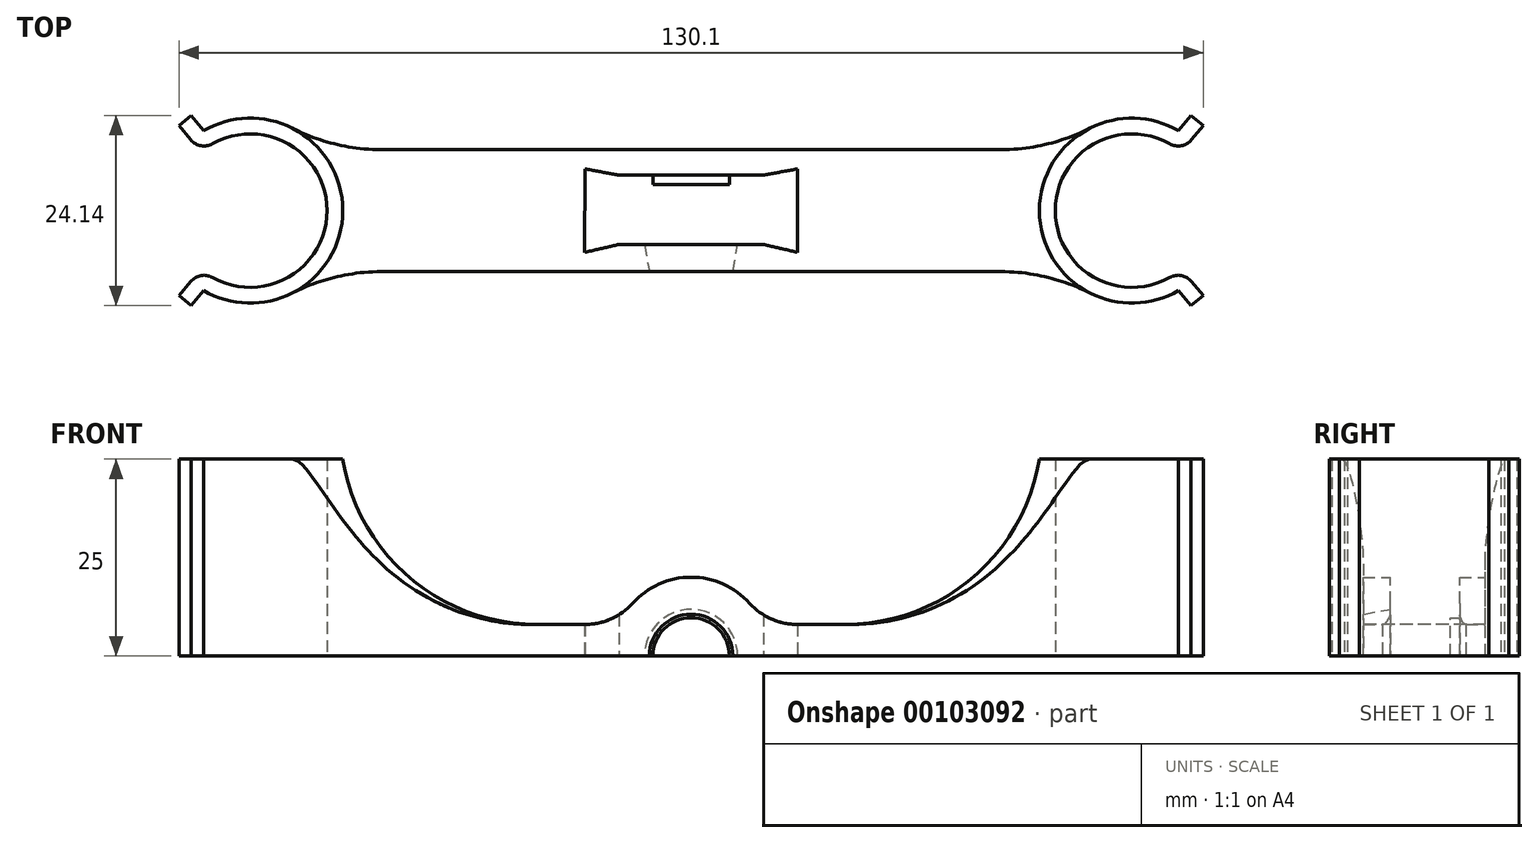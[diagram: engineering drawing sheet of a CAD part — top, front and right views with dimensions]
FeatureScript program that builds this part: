
annotation { "Feature Type Name" : "Feature", "Feature Type Description" : "" }
export const myFeature = defineFeature(function(context is Context, id is Id, definition is map)
    precondition{}
    {
        {
            var Q0;
            Q0=qCreatedBy(makeId("Top.planeOp"),FACE);
            var sketch = newSketch(context, id + "F0", { "sketchPlane" : qUnion([Q0])});
            skArc(sketch, "E0", {"start": v(-62.27, -7.47) * mm, "mid": v(-46.25, 0) * mm, "end": v(-62.27, 7.47) * mm});
            skLineSegment(sketch, "E1", {"start": v(-56, 0) * mm, "end": v(-68.54, -14.94) * mm, "construction": true});
            skLineSegment(sketch, "E2", {"start": v(-56, 0) * mm, "end": v(-67.56, 13.78) * mm, "construction": true});
            skArc(sketch, "E3", {"start": v(-63.55, -9) * mm, "mid": v(-44.25, 0) * mm, "end": v(-63.55, 9) * mm});
            skLineSegment(sketch, "E4", {"start": v(-63.55, 9) * mm, "end": v(-65.05, 10.78) * mm});
            skLineSegment(sketch, "E5", {"start": v(-65.05, 10.78) * mm, "end": v(-63.52, 12.07) * mm});
            skLineSegment(sketch, "E6", {"start": v(-63.52, 12.07) * mm, "end": v(-61.91, 10.16) * mm});
            skLineSegment(sketch, "E7", {"start": v(-54.18, 11.6) * mm, "end": v(-54.49, 9.63) * mm, "construction": true});
            skArc(sketch, "E8", {"start": v(-63.55, 9) * mm, "mid": v(-62.26, 8.25) * mm, "end": v(-60.78, 8.5) * mm});
            skLineSegment(sketch, "E9", {"start": v(-63.55, -9) * mm, "end": v(-65.05, -10.78) * mm});
            skLineSegment(sketch, "E10", {"start": v(-65.05, -10.78) * mm, "end": v(-63.52, -12.07) * mm});
            skLineSegment(sketch, "E11", {"start": v(-63.52, -12.07) * mm, "end": v(-61.91, -10.16) * mm});
            skArc(sketch, "E12", {"start": v(-60.78, -8.5) * mm, "mid": v(-62.26, -8.25) * mm, "end": v(-63.55, -9) * mm});
            skLineSegment(sketch, "E13.MirrorCS", {"start": v(65.05, -10.78) * mm, "end": v(63.52, -12.07) * mm});
            skLineSegment(sketch, "E14.MirrorCS", {"start": v(63.55, 9) * mm, "end": v(65.05, 10.78) * mm});
            skLineSegment(sketch, "E15.MirrorCS", {"start": v(63.52, -12.07) * mm, "end": v(61.91, -10.16) * mm});
            skLineSegment(sketch, "E16.MirrorCS", {"start": v(63.55, -9) * mm, "end": v(65.05, -10.78) * mm});
            skLineSegment(sketch, "E17.MirrorCS", {"start": v(65.05, 10.78) * mm, "end": v(63.52, 12.07) * mm});
            skLineSegment(sketch, "E18.MirrorCS", {"start": v(63.52, 12.07) * mm, "end": v(61.91, 10.16) * mm});
            skArc(sketch, "E19.MirrorCS", {"start": v(60.78, -8.5) * mm, "mid": v(62.26, -8.25) * mm, "end": v(63.55, -9) * mm});
            skArc(sketch, "E20.MirrorCS", {"start": v(63.55, 9) * mm, "mid": v(62.26, 8.25) * mm, "end": v(60.78, 8.5) * mm});
            skLineSegment(sketch, "E21.MirrorCS", {"start": v(54.18, 11.6) * mm, "end": v(54.49, 9.63) * mm, "construction": true});
            skArc(sketch, "E22.MirrorCS", {"start": v(62.27, -7.47) * mm, "mid": v(46.25, 0) * mm, "end": v(62.27, 7.47) * mm});
            skLineSegment(sketch, "E23.MirrorCS", {"start": v(56, 0) * mm, "end": v(68.54, -14.94) * mm, "construction": true});
            skLineSegment(sketch, "E24.MirrorCS", {"start": v(56, 0) * mm, "end": v(67.56, 13.78) * mm, "construction": true});
            skArc(sketch, "E25.MirrorCS", {"start": v(63.55, -9) * mm, "mid": v(44.25, 0) * mm, "end": v(63.55, 9) * mm});
            skSolve(sketch);
        }
        {
            var Q0;
            Q0 = qSketchRegion(id + "F0", true);
            extrude(context, id + "F1", {"entities" : qUnion([Q0]), "depth" : 25 * mm});
        }
        {
            var Q0;
            Q0=qCreatedBy(makeId("Top.planeOp"),FACE);
            var sketch = newSketch(context, id + "F2", { "sketchPlane" : qUnion([Q0])});
            skLineSegment(sketch, "E26.bottom", {"start": v(50.08, -7.75) * mm, "end": v(-50.08, -7.75) * mm});
            skLineSegment(sketch, "E26.top", {"start": v(50.08, 7.75) * mm, "end": v(-50.08, 7.75) * mm});
            skLineSegment(sketch, "E26.left", {"start": v(50.08, -7.75) * mm, "end": v(50.08, 7.75) * mm});
            skLineSegment(sketch, "E26.right", {"start": v(-50.08, -7.75) * mm, "end": v(-50.08, 7.75) * mm});
            skPoint(sketch, "E26.middle", {"position": v(0, 0) * mm});
            skSolve(sketch);
        }
        {
            var Q0;
            Q0 = qSketchRegion(id + "F2", true);
            extrude(context, id + "F3", {"entities" : qUnion([Q0]), "operationType" : NewBodyOperationType.ADD, "depth" : 4 * mm});
        }
        {
            var Q0;
            Q0=qCreatedBy(makeId("Top.planeOp"),FACE);
            var sketch = newSketch(context, id + "F4", { "sketchPlane" : qUnion([Q0])});
            skArc(sketch, "E27.0", {"start": v(-62.27, -7.47) * mm, "mid": v(-46.25, 0) * mm, "end": v(-62.27, 7.47) * mm});
            skArc(sketch, "E27.1", {"start": v(62.27, -7.47) * mm, "mid": v(46.25, 0) * mm, "end": v(62.27, 7.47) * mm});
            skLineSegment(sketch, "E28", {"start": v(-62.27, 7.47) * mm, "end": v(-62.27, -7.47) * mm});
            skLineSegment(sketch, "E29", {"start": v(62.27, 7.47) * mm, "end": v(62.27, -7.47) * mm});
            skSolve(sketch);
        }
        {
            var Q0;
            Q0 = qSketchRegion(id + "F4", true);
            extrude(context, id + "F5", {"entities" : qUnion([Q0]), "operationType" : NewBodyOperationType.REMOVE, "endBound" : BoundingType.THROUGH_ALL, "depth" : 25 * mm});
        }
        {
            var Q0;
            Q0=qCreatedBy(makeId("Front.planeOp"),FACE);
            var sketch = newSketch(context, id + "F6", { "sketchPlane" : qUnion([Q0])});
            skArc(sketch, "E30", {"start": v(10, 0) * mm, "mid": v(0, 10) * mm, "end": v(-10, 0) * mm});
            skLineSegment(sketch, "E31.0", {"start": v(47.17, 0) * mm, "end": v(-47.17, 0) * mm});
            skSolve(sketch);
        }
        {
            var Q0;
            Q0 = qSketchRegion(id + "F6", true);
            var Q1;
            Q1=makeQuery(id+"F3.opExtrude","SWEPT_FACE",FACE,{"disambiguationData":[OSD([sQuery(id+"F2.wireOp",EDGE,"E26.bottom")])]});
            var Q2;
            Q2=makeQuery(id+"F3.opExtrude","SWEPT_FACE",FACE,{"disambiguationData":[OSD([sQuery(id+"F2.wireOp",EDGE,"E26.top")])]});
            extrude(context, id + "F7", {"entities" : qUnion([Q0]), "operationType" : NewBodyOperationType.ADD, "endBound" : BoundingType.UP_TO_SURFACE, "endBoundEntityFace" : qUnion([Q1]), "depth" : 25 * mm, "hasSecondDirection" : true, "secondDirectionBound" : SecondDirectionBoundingType.UP_TO_SURFACE, "secondDirectionOppositeDirection" : true, "secondDirectionBoundEntityFace" : qUnion([Q2]), "secondDirectionDepth" : 25 * mm});
        }
        {
            var Q0;
            Q0=qCreatedBy(makeId("Top.planeOp"),FACE);
            var sketch = newSketch(context, id + "F8", { "sketchPlane" : qUnion([Q0])});
            skLineSegment(sketch, "E32.left", {"start": v(13.5, -5.3) * mm, "end": v(13.5, 5.3) * mm});
            skLineSegment(sketch, "E32.right", {"start": v(-13.5, -5.3) * mm, "end": v(-13.5, 5.3) * mm});
            skPoint(sketch, "E32.middle", {"position": v(0, 0) * mm});
            skLineSegment(sketch, "E33", {"start": v(9.17, 4.5) * mm, "end": v(-9.17, 4.5) * mm});
            skLineSegment(sketch, "E34", {"start": v(9.17, -4.3) * mm, "end": v(-9.17, -4.3) * mm});
            skLineSegment(sketch, "E35", {"start": v(-9.17, 4.5) * mm, "end": v(-13.5, 5.3) * mm});
            skLineSegment(sketch, "E36", {"start": v(-9.17, -4.3) * mm, "end": v(-13.5, -5.3) * mm});
            skLineSegment(sketch, "E37", {"start": v(9.17, 4.5) * mm, "end": v(13.5, 5.3) * mm});
            skLineSegment(sketch, "E38", {"start": v(9.17, -4.3) * mm, "end": v(13.5, -5.3) * mm});
            skPoint(sketch, "E39", {"position": v(-13.5, 0) * mm});
            skPoint(sketch, "E40", {"position": v(13.5, 0) * mm});
            skLineSegment(sketch, "E41.0", {"start": v(-9.17, -7.75) * mm, "end": v(-9.17, 7.75) * mm, "construction": true});
            skLineSegment(sketch, "E42.0", {"start": v(9.17, 7.75) * mm, "end": v(9.17, -7.75) * mm, "construction": true});
            skSolve(sketch);
        }
        {
            var Q0;
            Q0 = qSketchRegion(id + "F8", true);
            extrude(context, id + "F9", {"entities" : qUnion([Q0]), "operationType" : NewBodyOperationType.REMOVE, "endBound" : BoundingType.THROUGH_ALL, "depth" : 8.6 * mm});
        }
        {
            var Q0;
            {var subQ0=sQuery(id+"F2.wireOp",EDGE,"E26.bottom");Q0=makeQuery(id+"F7.boolean.opBoolean","MERGE",FACE,{"derivedFrom":[makeQuery(id+"F3.opExtrude","SWEPT_FACE",FACE,{"disambiguationData":[OSD([subQ0])]}),makeQuery(id+"F7.opExtrude","CAP_FACE",FACE,{"disambiguationData":[OSD([subQ0])],"isStart":false})]});}
            var sketch = newSketch(context, id + "F10", { "sketchPlane" : qUnion([Q0])});
            skCircle(sketch, "E43", {"center": v(0, 0) * mm, "radius": 5.3 * mm});
            skSolve(sketch);
        }
        {
            var Q0;
            Q0 = qSketchRegion(id + "F10", true);
            var Q1;
            Q1=makeQuery(id+"F9.boolean.opBoolean","COPY",FACE,{"derivedFrom":makeQuery(id+"F9.opExtrude","SWEPT_FACE",FACE,{"disambiguationData":[OSD([sQuery(id+"F8.wireOp",EDGE,"E34")])]})});
            extrude(context, id + "F11", {"entities" : qUnion([Q0]), "operationType" : NewBodyOperationType.REMOVE, "endBound" : BoundingType.UP_TO_SURFACE, "oppositeDirection" : true, "endBoundEntityFace" : qUnion([Q1]), "depth" : 25 * mm, "hasDraft" : true, "draftAngle" : 10 * degree});
        }
        {
            var Q0;
            Q0=makeQuery(id+"F9.boolean.opBoolean","COPY",FACE,{"derivedFrom":makeQuery(id+"F9.opExtrude","SWEPT_FACE",FACE,{"disambiguationData":[OSD([sQuery(id+"F8.wireOp",EDGE,"E33")])]})});
            var sketch = newSketch(context, id + "F12", { "sketchPlane" : qUnion([Q0])});
            skArc(sketch, "E44", {"start": v(4.85, 0) * mm, "mid": v(0, 4.85) * mm, "end": v(-4.85, 0) * mm});
            skLineSegment(sketch, "E45.0", {"start": v(9.17, 0) * mm, "end": v(-9.17, 0) * mm});
            skSolve(sketch);
        }
        {
            var Q0;
            Q0 = qSketchRegion(id + "F12", true);
            extrude(context, id + "F13", {"entities" : qUnion([Q0]), "operationType" : NewBodyOperationType.ADD, "depth" : 1.2 * mm});
        }
        {
            var Q0;
            {var subQ0=makeQuery(id+"F7.opExtrude","SWEPT_FACE",FACE,{"disambiguationData":[OSD([sQuery(id+"F6.wireOp",EDGE,"E30")])]});var subQ1=sQuery(id+"F2.wireOp",EDGE,"E26.top");var subQ2=makeQuery(id+"F3.opExtrude","CAP_FACE",FACE,{"disambiguationData":[OSD([sQuery(id+"F2.wireOp",EDGE,"E26.bottom"),subQ1,sQuery(id+"F2.wireOp",EDGE,"E26.left"),sQuery(id+"F2.wireOp",EDGE,"E26.right")])],"isStart":false});Q0=makeQuery(id+"F9.boolean.opBoolean","SPLIT",EDGE,{"disambiguationData":[TD([makeQuery(id+"F3.opExtrude","SWEPT_FACE",FACE,{"disambiguationData":[OSD([subQ1])]})])],"derivedFrom":makeQuery(id+"F7.boolean.opBoolean","INTERSECT",EDGE,{"disambiguationData":[OD(1.0)],"derivedFrom":[subQ2,subQ0]})});}
            var Q1;
            {var subQ0=sQuery(id+"F2.wireOp",EDGE,"E26.bottom");var subQ1=makeQuery(id+"F3.opExtrude","CAP_FACE",FACE,{"disambiguationData":[OSD([subQ0,sQuery(id+"F2.wireOp",EDGE,"E26.top"),sQuery(id+"F2.wireOp",EDGE,"E26.left"),sQuery(id+"F2.wireOp",EDGE,"E26.right")])],"isStart":false});var subQ2=makeQuery(id+"F7.opExtrude","SWEPT_FACE",FACE,{"disambiguationData":[OSD([sQuery(id+"F6.wireOp",EDGE,"E30")])]});Q1=makeQuery(id+"F9.boolean.opBoolean","SPLIT",EDGE,{"disambiguationData":[TD([makeQuery(id+"F3.opExtrude","SWEPT_FACE",FACE,{"disambiguationData":[OSD([subQ0])]})])],"derivedFrom":makeQuery(id+"F7.boolean.opBoolean","INTERSECT",EDGE,{"disambiguationData":[OD(1.0)],"derivedFrom":[subQ1,subQ2]})});}
            var Q2;
            {var subQ0=sQuery(id+"F2.wireOp",EDGE,"E26.bottom");var subQ1=makeQuery(id+"F3.opExtrude","CAP_FACE",FACE,{"disambiguationData":[OSD([subQ0,sQuery(id+"F2.wireOp",EDGE,"E26.top"),sQuery(id+"F2.wireOp",EDGE,"E26.left"),sQuery(id+"F2.wireOp",EDGE,"E26.right")])],"isStart":false});var subQ2=makeQuery(id+"F7.opExtrude","SWEPT_FACE",FACE,{"disambiguationData":[OSD([sQuery(id+"F6.wireOp",EDGE,"E30")])]});Q2=makeQuery(id+"F9.boolean.opBoolean","SPLIT",EDGE,{"disambiguationData":[TD([makeQuery(id+"F3.opExtrude","SWEPT_FACE",FACE,{"disambiguationData":[OSD([subQ0])]})])],"derivedFrom":makeQuery(id+"F7.boolean.opBoolean","INTERSECT",EDGE,{"disambiguationData":[OD(0.0)],"derivedFrom":[subQ1,subQ2]})});}
            var Q3;
            {var subQ0=makeQuery(id+"F7.opExtrude","SWEPT_FACE",FACE,{"disambiguationData":[OSD([sQuery(id+"F6.wireOp",EDGE,"E30")])]});var subQ1=sQuery(id+"F2.wireOp",EDGE,"E26.top");var subQ2=makeQuery(id+"F3.opExtrude","CAP_FACE",FACE,{"disambiguationData":[OSD([sQuery(id+"F2.wireOp",EDGE,"E26.bottom"),subQ1,sQuery(id+"F2.wireOp",EDGE,"E26.left"),sQuery(id+"F2.wireOp",EDGE,"E26.right")])],"isStart":false});Q3=makeQuery(id+"F9.boolean.opBoolean","SPLIT",EDGE,{"disambiguationData":[TD([makeQuery(id+"F3.opExtrude","SWEPT_FACE",FACE,{"disambiguationData":[OSD([subQ1])]})])],"derivedFrom":makeQuery(id+"F7.boolean.opBoolean","INTERSECT",EDGE,{"disambiguationData":[OD(0.0)],"derivedFrom":[subQ2,subQ0]})});}
            fillet(context, id + "F14", {"entities" : qUnion([Q0, Q1, Q2, Q3]), "radius" : 8.1 * mm, "tangentPropagation" : true, "allowEdgeOverflow" : false});
        }
        {
            var Q0;
            Q0=makeQuery(id+"F3.boolean.opBoolean","INTERSECT",EDGE,{"derivedFrom":[makeQuery(id+"F1.opExtrude","SWEPT_FACE",FACE,{"disambiguationData":[OSD([sQuery(id+"F0.wireOp",EDGE,"E25.MirrorCS")])]}),makeQuery(id+"F3.opExtrude","CAP_FACE",FACE,{"disambiguationData":[OSD([sQuery(id+"F2.wireOp",EDGE,"E26.bottom"),sQuery(id+"F2.wireOp",EDGE,"E26.top"),sQuery(id+"F2.wireOp",EDGE,"E26.left"),sQuery(id+"F2.wireOp",EDGE,"E26.right")])],"isStart":false})]});
            var Q1;
            Q1=makeQuery(id+"F3.boolean.opBoolean","INTERSECT",EDGE,{"derivedFrom":[makeQuery(id+"F1.opExtrude","SWEPT_FACE",FACE,{"disambiguationData":[OSD([sQuery(id+"F0.wireOp",EDGE,"E3")])]}),makeQuery(id+"F3.opExtrude","CAP_FACE",FACE,{"disambiguationData":[OSD([sQuery(id+"F2.wireOp",EDGE,"E26.bottom"),sQuery(id+"F2.wireOp",EDGE,"E26.top"),sQuery(id+"F2.wireOp",EDGE,"E26.left"),sQuery(id+"F2.wireOp",EDGE,"E26.right")])],"isStart":false})]});
            fillet(context, id + "F15", {"entities" : qUnion([Q0, Q1]), "radius" : 25 * mm, "tangentPropagation" : true, "allowEdgeOverflow" : false});
        }
        {
            var Q0;
            Q0=makeQuery(id+"F3.boolean.opBoolean","INTERSECT",EDGE,{"derivedFrom":[makeQuery(id+"F1.opExtrude","SWEPT_FACE",FACE,{"disambiguationData":[OSD([sQuery(id+"F0.wireOp",EDGE,"E3")])]}),makeQuery(id+"F3.opExtrude","SWEPT_FACE",FACE,{"disambiguationData":[OSD([sQuery(id+"F2.wireOp",EDGE,"E26.bottom")])]})]});
            var Q1;
            Q1=makeQuery(id+"F3.boolean.opBoolean","INTERSECT",EDGE,{"derivedFrom":[makeQuery(id+"F1.opExtrude","SWEPT_FACE",FACE,{"disambiguationData":[OSD([sQuery(id+"F0.wireOp",EDGE,"E3")])]}),makeQuery(id+"F3.opExtrude","SWEPT_FACE",FACE,{"disambiguationData":[OSD([sQuery(id+"F2.wireOp",EDGE,"E26.top")])]})]});
            var Q2;
            Q2=makeQuery(id+"F3.boolean.opBoolean","INTERSECT",EDGE,{"derivedFrom":[makeQuery(id+"F1.opExtrude","SWEPT_FACE",FACE,{"disambiguationData":[OSD([sQuery(id+"F0.wireOp",EDGE,"E25.MirrorCS")])]}),makeQuery(id+"F3.opExtrude","SWEPT_FACE",FACE,{"disambiguationData":[OSD([sQuery(id+"F2.wireOp",EDGE,"E26.top")])]})]});
            var Q3;
            Q3=makeQuery(id+"F3.boolean.opBoolean","INTERSECT",EDGE,{"derivedFrom":[makeQuery(id+"F1.opExtrude","SWEPT_FACE",FACE,{"disambiguationData":[OSD([sQuery(id+"F0.wireOp",EDGE,"E25.MirrorCS")])]}),makeQuery(id+"F3.opExtrude","SWEPT_FACE",FACE,{"disambiguationData":[OSD([sQuery(id+"F2.wireOp",EDGE,"E26.bottom")])]})]});
            fillet(context, id + "F16", {"entities" : qUnion([Q0, Q1, Q2, Q3]), "radius" : 25 * mm, "tangentPropagation" : true, "allowEdgeOverflow" : false});
        }
    });
